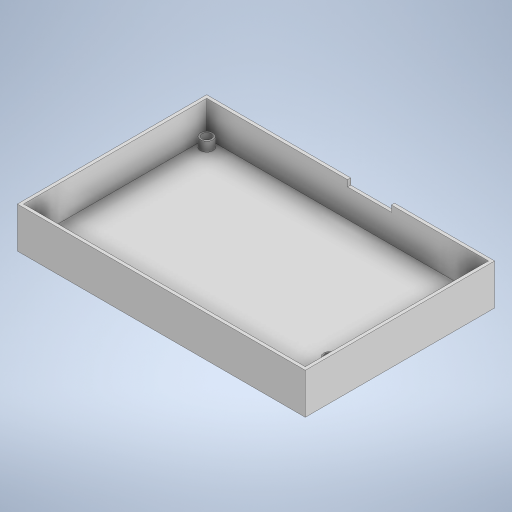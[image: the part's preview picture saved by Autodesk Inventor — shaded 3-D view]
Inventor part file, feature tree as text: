
AUTODESK INVENTOR PART (.ipt)
format: ipt  version: 2023 (Build 270158000, 158)  size: 637,952 bytes
history: native  units: mm
features: extrude x4, sketch x3, other x1, imported_body x1
ambient origin geometry x8: Origin, YZ Plane, XZ Plane, XY Plane, X Axis, Y Axis, Z Axis, Center Point
bodies: Body1 (feature_tree)
feature tree (9):
  other  "Sólido1"
  extrude  "Extrusão1"  Depth=121.0mm
  extrude  "Extrusão2"  Depth=180.0mm
  extrude  "Extrusão3"  Depth=22.0mm TaperAngle=0.0deg
  extrude  "Extrusão4"  Depth=6.0mm
  imported_body  "Base"
  sketch  "Esboço2"  dims[d0=184.0mm d1=121.0mm]
  sketch  "Esboço3"  dims[d2=26.0mm d3=0.0mm d4=180.0mm]
  sketch  "Esboço4"  dims[d5=117.0mm d6=22.0mm d7=0.0mm d8=8.0mm d9=7.0mm d10=7.0mm d11=6.0mm d12=7.0mm d13=7.0mm d14=8.0mm d15=31.51mm d16=15.73mm d17=6.0mm d18=6.0mm d19=0.0mm d20=120.0mm d21=28.0mm d22=0.0mm d24=4.0mm d25=4.0mm d26=2.0mm d27=0.0mm d28=0.0mm d29=6.0mm d30=8.0mm d31=8.0mm d32=6.0mm]
